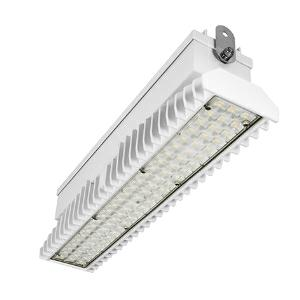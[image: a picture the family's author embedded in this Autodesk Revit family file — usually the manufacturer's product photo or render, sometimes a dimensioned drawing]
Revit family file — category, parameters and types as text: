
# Revit family: 3f_filippi_-_3f_lem_ho_concentrato_3f_filippi_-_58959_a0811_-_3f_lem_1_ho_led_70_cr_conc___vt_cdb4
name_source: partatom
category: Lighting Fixtures
units: mm (PartAtom-declared; Revit-internal decimal feet)

## family parameters
Cut with Voids When Loaded = No
Host = Face
Light Source = No
Part Type = Normal
Room Calculation Point = No
Round Connector Dimension = Use Diameter
Shared = No

## types (1)
- 3F Filippi - 3F LEM HO Concentrato (1 x LED, 10083 lm, 71 W, 4000 K)
    Apparent Load = 71 VA
    Approval mark = CE
    CIE Flux Codes = 83 96 99 100 100
    Color Rendering = 80
    Color Temperature = 4000 K
    Control Gear = Electronic ballast
    Default Elevation = 1800 mm
    Description = Industrial luminaire with high light output and high luminous efficiency designed with the most innovative technologies for environments with temperature up to 55°C.

ILLUMINOTECHNICAL
Luminous efficiency 100% (DLOR 99%, ULOR 1%).
Initial luminous flux of the luminaire 10083 lm.
Direct symmetric narrow distribution: the illuminated area has a elliptical shape.
Installation Interdistance Transv.D = 0.52 x hu - Long.D = 1.16 x hu.
Tabular UGR (CIE 117 - 4H-8H; S=0.25H; 70/50/20): RUG 21.2 - 25.
Beam angle: 31° - 73°.
Luminous efficacy 142 lm/W.
Lifetime (L93/B10): 30000 h. (tq+25°C)
Lifetime (L90/B10): 50000 h. (tq+25°C)
Lifetime (L85/B10): 80000 h. (tq+25°C)
Lifetime (L80/B10): 100000 h. (tq+25°C)
Lifetime (L85/B10): 50000 h. (tq+55°C)
Sudden decreased luminous flux after 50000 hours: 0% (C0).
Photobiological safety in compliance with IEC/TR 62778: RG0 risk exempt, (IEC 62471).
In compliance with IEC/EN 62722-2-1 - IEC/EN 62717 standards.

SOURCE
Mid-Power linear LED module 70W/840.
Energy efficiency class (UE 2019/2020 - UE 2019/2015): C.
CIE 13.3 Colour rendering index: CRI >80 (R9 <50%).
IES TM-30 Fidelity Index: Rf = 84 Rg = 95.
CCT nominal colour temperature 4000 K.
Colour initial tolerance (MacAdam): SDCM 3.

MECHANICAL
Passive modular heatsinks in die-casted aluminium, painted in white colour.
To optimize the thermal management of the LED module, the heatsinks are oversized and provided with self-cleaning of cooling fins.
Wiring body in aluminium and galvanised steel anchored solidly to the sinks and thermally separated.
3F Lens lenses with high luminous efficiency, transparent methacrylate (PMMA), fixed to the LED modules.
Fixing brackets in stainless steel.
Luminaire with limited surface temperature. - D - (EN 60598-2-24)
Dimensions: 542x115 mm, height 154 mm. Weight 6.372 kg.
IP65 protection degree.
Mechanical strength to impacts IK06 (1 joule).
Glow-wire test resistance 650°C.

ELECTRICAL
Halogen Free electronic wiring 230V-50/60Hz, power factor 0.97, THD <25%, constant output current, class I, 1 driver.
Power of the luminaire 71 W.
ENEC - CE.
SAFE FLICKER: PstLM=<1 and SVM=<0.4 (IEC TR 61547-1 and IEC TR 63158), to ensure a more comfortable and safe light.
Luminaire compliant with EN 60598-2-22 for power supply from a centralised emergency system CPSS (Central Power Supply System), not incorporated in the luminaire - high risk areas excluded. The default power and flux are 100% in AC and 100% in DC.
Ambient temperature from -30°C to +55°C.
Temperature class T6 max 85°C.
Quick connection via M20 3P connector with 9-13 mm tightening range.
Power unit positioned on a separate compartment by the LED module to ensure optimum temperatures of cabling components, to be inspectable and maintainable.
Relative humidity UR: <85%.

INSTALLATION
Ceiling / Suspended / Wall.
All accessories dedicated to this product are available on the Catalog and on our website www.3F-Filippi.com.

ACCESSORIES
A0811 - VT transparent glass, tempered, not flammable, with sealing gasket.
One required for each light module. The pack contains 10 pieces.

APPLICATIONS
In commercial environments, exhibition and industrial areas, stores, open areas or with shelves.
Environments in which it is necessary a total protection against falling fragments (eg environments with foodstuffs or machines with moving parts or with extreme temperature changes), use luminaires with polycarbonate lenses.

WARNING
Fixture not suitable for cold stores with an ambient temperature <0°C and/or relative humidity >85%.
Luminaire designed for disposal/recycling at end-of-life.
Replaceable (LED only) light source by a professional. Replaceable control gear by a professional.
    Height = 154 mm
    Lamp = 1 x LED
    Lamp Light Flux = 10083 lm
    Lamp Power = 71 W
    Lamp count = 1
    Length = 542 mm
    Lifetime = 50000 h
    Luminous efficacy = 142 lm/W
    Manufacturer = 3F Filippi
    ModVariant = No
    Model = 3F Filippi - 58959+A0811 - 3F LEM 1 HO LED 70 CR CONC + VT
    Mounting Place = Ceiling
    Mounting Type = Pendant
    Number of Poles = 1
    OnlyDefault = Yes
    Power Factor = 1
    Product Name = 3F Filippi - 3F LEM HO Concentrato
    Product group = pendant luminaire
    ProductGroupID = 9
    Protection Class = Protection class I
    Protection Degree = IP 65
    RLX_Detail_Level = 1
    RLX_Emergency_Light_Flux = 0 lm
    RLX_Emergency_Type = 0
    RLX_Emergency_Type_DB = No
    RlxData = <blob elided: 94657 chars, md5=84a701cc>
    Socket = socket
    Standby Power = 0 W
    System Light Flux = 10083 lm
    System Power = 71 W
    Type Comments = Product without accessories
    Type Image = 3f_filippi_-_lem_1__a0811.jpg
    URL = http://relux.com
    VarID = ---
    Voltage = 0 V
    Weight = 0.00 kg
    Width = 115 mm

## geometry (parser evidence)
native form markers: Blend x4, Sweep x14
no freeform markers — native parametric forms only
